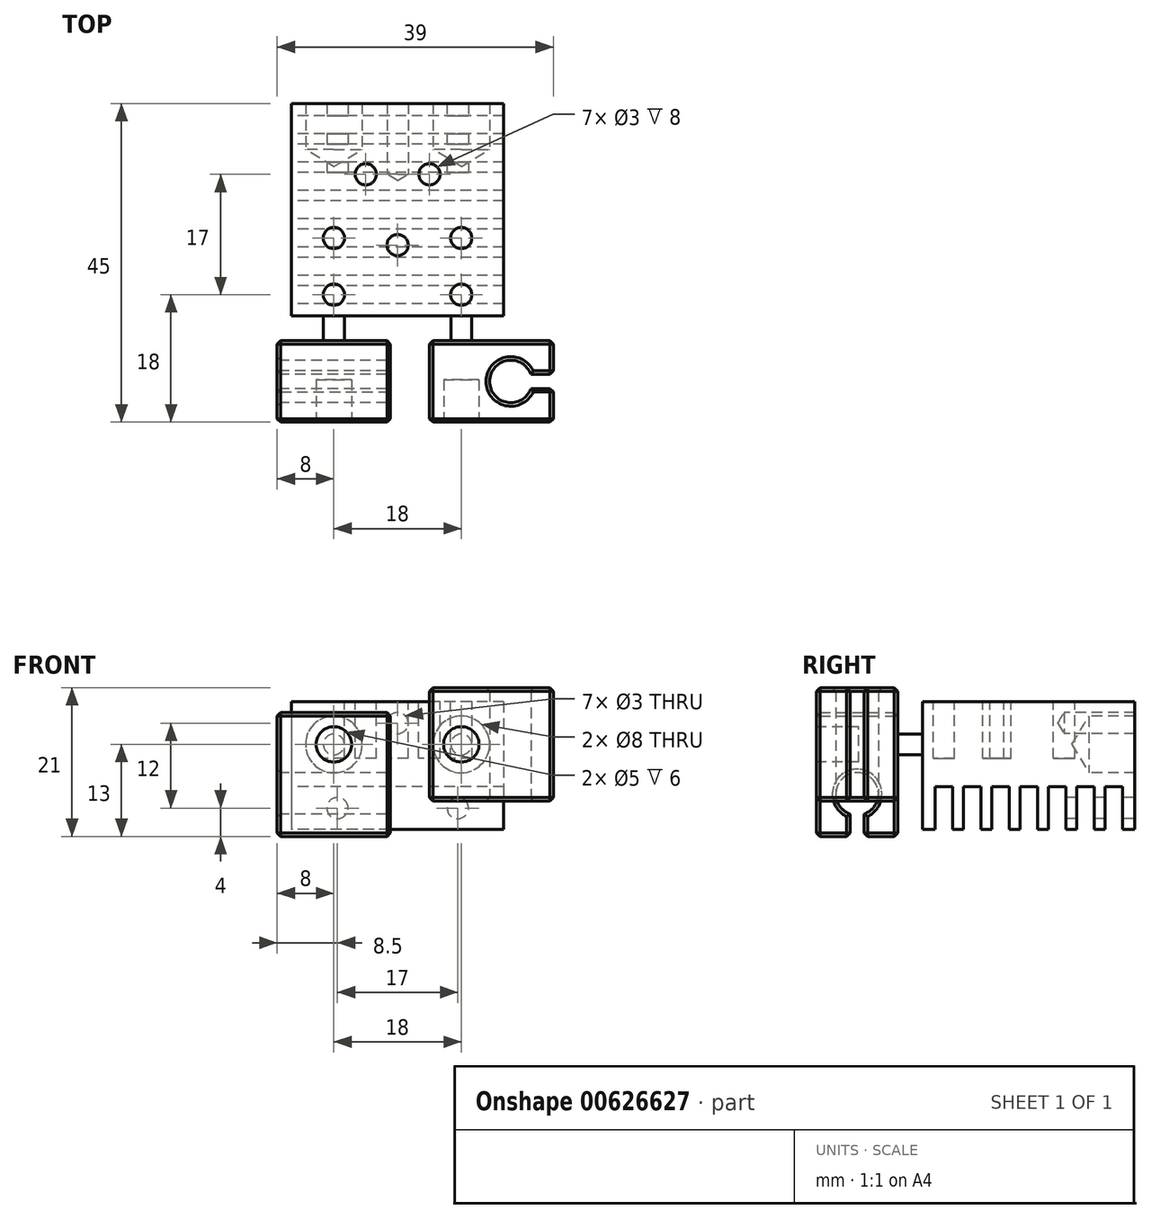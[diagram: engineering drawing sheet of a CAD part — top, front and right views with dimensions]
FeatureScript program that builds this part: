
annotation { "Feature Type Name" : "Feature", "Feature Type Description" : "" }
export const myFeature = defineFeature(function(context is Context, id is Id, definition is map)
    precondition{}
    {
        {
            var Q0;
            Q0=qCreatedBy(makeId("Top.planeOp"),FACE);
            var sketch = newSketch(context, id + "F0", { "sketchPlane" : qUnion([Q0])});
            skLineSegment(sketch, "E0.bottom", {"start": v(15, -15) * mm, "end": v(-15, -15) * mm});
            skLineSegment(sketch, "E0.top", {"start": v(15, 15) * mm, "end": v(-15, 15) * mm});
            skLineSegment(sketch, "E0.left", {"start": v(15, -15) * mm, "end": v(15, 15) * mm});
            skLineSegment(sketch, "E0.right", {"start": v(-15, -15) * mm, "end": v(-15, 15) * mm});
            skPoint(sketch, "E0.middle", {"position": v(0, 0) * mm});
            skSolve(sketch);
        }
        {
            var Q0;
            Q0=makeQuery(id+"F0.imprint","IMPRINT",FACE,{"disambiguationData":[TD([[makeQuery(id+"F0.imprint","IMPRINT",EDGE,{"derivedFrom":sQuery(id+"F0.wireOp",EDGE,"E0.bottom")}),-1.0]])]});
            extrude(context, id + "F11", {"entities" : qUnion([Q0]), "depth" : 18 * mm});
        }
        {
            var Q0;
            Q0=makeQuery(id+"F11.opExtrude","SWEPT_FACE",FACE,{"disambiguationData":[OSD([sQuery(id+"F0.wireOp",EDGE,"E0.top")])]});
            var sketch = newSketch(context, id + "F12", { "sketchPlane" : qUnion([Q0])});
            skPoint(sketch, "E1", {"position": v(-8.5, 3) * mm});
            skPoint(sketch, "E2", {"position": v(8.5, 3) * mm});
            skPoint(sketch, "E3", {"position": v(-9, 12) * mm});
            skPoint(sketch, "E4", {"position": v(9, 12) * mm});
            skPoint(sketch, "E5", {"position": v(0, 15) * mm});
            skSolve(sketch);
        }
        {
            var Q0;
            Q0=sQuery(id+"F12.wireOp",VERTEX,"E3");
            var Q1;
            Q1=sQuery(id+"F12.wireOp",VERTEX,"E4");
            var Q2;
            Q2=makeQuery(id+"F11.opExtrude","SWEPT_BODY",BODY,{"disambiguationData":[OSD([sQuery(id+"F0.wireOp",EDGE,"E0.bottom"),sQuery(id+"F0.wireOp",EDGE,"E0.top"),sQuery(id+"F0.wireOp",EDGE,"E0.left"),sQuery(id+"F0.wireOp",EDGE,"E0.right")])]});
            hole(context, id + "F1", {"style" : HoleStyle.SIMPLE, "endStyle" : HoleEndStyle.BLIND, "holeDiameter" : 8 * mm, "holeDepth" : 6.5 * mm, "locations" : qUnion([Q0, Q1]), "scope" : qUnion([Q2]), "tappedDepth" : 12 * mm, "tapClearance" : 3});
        }
        {
            var Q0;
            Q0=makeQuery(id+"F11.opExtrude","CAP_FACE",FACE,{"disambiguationData":[OSD([sQuery(id+"F0.wireOp",EDGE,"E0.bottom"),sQuery(id+"F0.wireOp",EDGE,"E0.top"),sQuery(id+"F0.wireOp",EDGE,"E0.left"),sQuery(id+"F0.wireOp",EDGE,"E0.right")])],"isStart":true});
            var sketch = newSketch(context, id + "F13", { "sketchPlane" : qUnion([Q0])});
            skLineSegment(sketch, "E6.bottom", {"start": v(15, -13.25) * mm, "end": v(-15.01, -13.25) * mm});
            skLineSegment(sketch, "E6.top", {"start": v(15, -10.75) * mm, "end": v(-15.01, -10.75) * mm});
            skLineSegment(sketch, "E6.left", {"start": v(15, -13.25) * mm, "end": v(15, -10.75) * mm});
            skLineSegment(sketch, "E6.right", {"start": v(-15.01, -13.25) * mm, "end": v(-15.01, -10.75) * mm});
            skLineSegment(sketch, "E7.0.1.0", {"start": v(15, -9.25) * mm, "end": v(15, -6.75) * mm});
            skLineSegment(sketch, "E7.0.1.1", {"start": v(-15.01, -9.25) * mm, "end": v(-15.01, -6.75) * mm});
            skLineSegment(sketch, "E7.0.1.2", {"start": v(15, -9.25) * mm, "end": v(-15.01, -9.25) * mm});
            skLineSegment(sketch, "E7.0.1.3", {"start": v(15, -6.75) * mm, "end": v(-15.01, -6.75) * mm});
            skLineSegment(sketch, "E7.0.2.0", {"start": v(15, -5.25) * mm, "end": v(15, -2.75) * mm});
            skLineSegment(sketch, "E7.0.2.1", {"start": v(-15.01, -5.25) * mm, "end": v(-15.01, -2.75) * mm});
            skLineSegment(sketch, "E7.0.2.2", {"start": v(15, -5.25) * mm, "end": v(-15.01, -5.25) * mm});
            skLineSegment(sketch, "E7.0.2.3", {"start": v(15, -2.75) * mm, "end": v(-15.01, -2.75) * mm});
            skLineSegment(sketch, "E7.0.3.0", {"start": v(15, -1.25) * mm, "end": v(15, 1.25) * mm});
            skLineSegment(sketch, "E7.0.3.1", {"start": v(-15.01, -1.25) * mm, "end": v(-15.01, 1.25) * mm});
            skLineSegment(sketch, "E7.0.3.2", {"start": v(15, -1.25) * mm, "end": v(-15.01, -1.25) * mm});
            skLineSegment(sketch, "E7.0.3.3", {"start": v(15, 1.25) * mm, "end": v(-15.01, 1.25) * mm});
            skLineSegment(sketch, "E7.0.4.0", {"start": v(15, 2.75) * mm, "end": v(15, 5.25) * mm});
            skLineSegment(sketch, "E7.0.4.1", {"start": v(-15.01, 2.75) * mm, "end": v(-15.01, 5.25) * mm});
            skLineSegment(sketch, "E7.0.4.2", {"start": v(15, 2.75) * mm, "end": v(-15.01, 2.75) * mm});
            skLineSegment(sketch, "E7.0.4.3", {"start": v(15, 5.25) * mm, "end": v(-15.01, 5.25) * mm});
            skLineSegment(sketch, "E7.0.5.0", {"start": v(15, 6.75) * mm, "end": v(15, 9.25) * mm});
            skLineSegment(sketch, "E7.0.5.1", {"start": v(-15.01, 6.75) * mm, "end": v(-15.01, 9.25) * mm});
            skLineSegment(sketch, "E7.0.5.2", {"start": v(15, 6.75) * mm, "end": v(-15.01, 6.75) * mm});
            skLineSegment(sketch, "E7.0.5.3", {"start": v(15, 9.25) * mm, "end": v(-15.01, 9.25) * mm});
            skLineSegment(sketch, "E7.0.6.0", {"start": v(15, 10.75) * mm, "end": v(15, 13.25) * mm});
            skLineSegment(sketch, "E7.0.6.1", {"start": v(-15.01, 10.75) * mm, "end": v(-15.01, 13.25) * mm});
            skLineSegment(sketch, "E7.0.6.2", {"start": v(15, 10.75) * mm, "end": v(-15.01, 10.75) * mm});
            skLineSegment(sketch, "E7.0.6.3", {"start": v(15, 13.25) * mm, "end": v(-15.01, 13.25) * mm});
            skLineSegment(sketch, "E7.direction1", {"start": v(-15.01, -13.25) * mm, "end": v(9.99, -13.25) * mm, "construction": true});
            skLineSegment(sketch, "E7.direction2", {"start": v(-15.01, -13.25) * mm, "end": v(-15.01, -9.25) * mm, "construction": true});
            skSolve(sketch);
        }
        {
            var Q0;
            {var subQ0=sQuery(id+"F13.wireOp",EDGE,"E7.0.6.0");Q0=makeQuery(id+"F13.imprint","IMPRINT",FACE,{"disambiguationData":[TD([[makeQuery(id+"F13.imprint","IMPRINT",EDGE,{"derivedFrom":subQ0}),-1.0]])]});}
            var Q1;
            {var subQ0=sQuery(id+"F13.wireOp",EDGE,"E7.0.5.0");Q1=makeQuery(id+"F13.imprint","IMPRINT",FACE,{"disambiguationData":[TD([[makeQuery(id+"F13.imprint","IMPRINT",EDGE,{"derivedFrom":subQ0}),-1.0]])]});}
            var Q2;
            {var subQ0=sQuery(id+"F13.wireOp",EDGE,"E7.0.4.0");Q2=makeQuery(id+"F13.imprint","IMPRINT",FACE,{"disambiguationData":[TD([[makeQuery(id+"F13.imprint","IMPRINT",EDGE,{"derivedFrom":subQ0}),-1.0]])]});}
            var Q3;
            {var subQ0=sQuery(id+"F13.wireOp",EDGE,"E7.0.3.0");Q3=makeQuery(id+"F13.imprint","IMPRINT",FACE,{"disambiguationData":[TD([[makeQuery(id+"F13.imprint","IMPRINT",EDGE,{"derivedFrom":subQ0}),-1.0]])]});}
            var Q4;
            {var subQ0=sQuery(id+"F13.wireOp",EDGE,"E7.0.2.0");Q4=makeQuery(id+"F13.imprint","IMPRINT",FACE,{"disambiguationData":[TD([[makeQuery(id+"F13.imprint","IMPRINT",EDGE,{"derivedFrom":subQ0}),-1.0]])]});}
            var Q5;
            {var subQ0=sQuery(id+"F13.wireOp",EDGE,"E7.0.1.0");Q5=makeQuery(id+"F13.imprint","IMPRINT",FACE,{"disambiguationData":[TD([[makeQuery(id+"F13.imprint","IMPRINT",EDGE,{"derivedFrom":subQ0}),-1.0]])]});}
            var Q6;
            {var subQ0=sQuery(id+"F13.wireOp",EDGE,"E6.left");Q6=makeQuery(id+"F13.imprint","IMPRINT",FACE,{"disambiguationData":[TD([[makeQuery(id+"F13.imprint","IMPRINT",EDGE,{"derivedFrom":subQ0}),-1.0]])]});}
            extrude(context, id + "F14", {"entities" : qUnion([Q0, Q1, Q2, Q3, Q4, Q5, Q6]), "operationType" : NewBodyOperationType.REMOVE, "oppositeDirection" : true, "depth" : 6 * mm});
        }
        {
            var Q0;
            Q0=sQuery(id+"F12.wireOp",VERTEX,"E2");
            var Q1;
            Q1=sQuery(id+"F12.wireOp",VERTEX,"E1");
            var Q2;
            Q2=sQuery(id+"F12.wireOp",VERTEX,"E5");
            var Q3;
            Q3=makeQuery(id+"F11.opExtrude","SWEPT_BODY",BODY,{"disambiguationData":[OSD([sQuery(id+"F0.wireOp",EDGE,"E0.bottom"),sQuery(id+"F0.wireOp",EDGE,"E0.top"),sQuery(id+"F0.wireOp",EDGE,"E0.left"),sQuery(id+"F0.wireOp",EDGE,"E0.right")])]});
            hole(context, id + "F15", {"style" : HoleStyle.SIMPLE, "endStyle" : HoleEndStyle.BLIND, "holeDiameter" : 3 * mm, "holeDepth" : 10 * mm, "locations" : qUnion([Q0, Q1, Q2]), "scope" : qUnion([Q3])});
        }
        {
            var Q0;
            Q0=makeQuery(id+"F11.opExtrude","SWEPT_FACE",FACE,{"disambiguationData":[OSD([sQuery(id+"F0.wireOp",EDGE,"E0.bottom")])]});
            var sketch = newSketch(context, id + "F2", { "sketchPlane" : qUnion([Q0])});
            skCircle(sketch, "E8", {"center": v(9, 12) * mm, "radius": 1.48 * mm});
            skCircle(sketch, "E9", {"center": v(-9, 12) * mm, "radius": 1.48 * mm});
            skLineSegment(sketch, "E10", {"start": v(-15, 12) * mm, "end": v(15, 12) * mm, "construction": true});
            skSolve(sketch);
        }
        {
            var Q0;
            Q0=makeQuery(id+"F2.imprint","IMPRINT",FACE,{"disambiguationData":[TD([[makeQuery(id+"F2.imprint","IMPRINT",EDGE,{"derivedFrom":sQuery(id+"F2.wireOp",EDGE,"E9")}),1.0]])]});
            var Q1;
            Q1=makeQuery(id+"F2.imprint","IMPRINT",FACE,{"disambiguationData":[TD([[makeQuery(id+"F2.imprint","IMPRINT",EDGE,{"derivedFrom":sQuery(id+"F2.wireOp",EDGE,"E8")}),1.0]])]});
            extrude(context, id + "F3", {"entities" : qUnion([Q0, Q1]), "operationType" : NewBodyOperationType.ADD, "depth" : 3.5 * mm});
        }
        {
            var Q0;
            Q0=makeQuery(id+"F3.opExtrude","CAP_FACE",FACE,{"disambiguationData":[OSD([sQuery(id+"F2.wireOp",EDGE,"E8")])],"isStart":false});
            var sketch = newSketch(context, id + "F16", { "sketchPlane" : qUnion([Q0])});
            skLineSegment(sketch, "E11.bottom", {"start": v(22, 20) * mm, "end": v(22, 4) * mm});
            skLineSegment(sketch, "E11.top", {"start": v(4.5, 20) * mm, "end": v(4.5, 4) * mm});
            skLineSegment(sketch, "E11.left", {"start": v(22, 20) * mm, "end": v(4.5, 20) * mm});
            skLineSegment(sketch, "E11.right", {"start": v(22, 4) * mm, "end": v(4.5, 4) * mm});
            skPoint(sketch, "E12", {"position": v(9, 12) * mm});
            skLineSegment(sketch, "E13", {"start": v(4.5, 12) * mm, "end": v(22, 12) * mm, "construction": true});
            skSolve(sketch);
        }
        {
            var Q0;
            Q0=makeQuery(id+"F3.opExtrude","CAP_FACE",FACE,{"disambiguationData":[OSD([sQuery(id+"F2.wireOp",EDGE,"E9")])],"isStart":false});
            var sketch = newSketch(context, id + "F17", { "sketchPlane" : qUnion([Q0])});
            skPoint(sketch, "E14", {"position": v(-9, 12) * mm});
            skLineSegment(sketch, "E15.bottom", {"start": v(-17, 16.5) * mm, "end": v(-1, 16.5) * mm});
            skLineSegment(sketch, "E15.top", {"start": v(-17, -1) * mm, "end": v(-1, -1) * mm});
            skLineSegment(sketch, "E15.left", {"start": v(-17, 16.5) * mm, "end": v(-17, -1) * mm});
            skLineSegment(sketch, "E15.right", {"start": v(-1, 16.5) * mm, "end": v(-1, -1) * mm});
            skLineSegment(sketch, "E16", {"start": v(-9, 16.5) * mm, "end": v(-9, -1) * mm, "construction": true});
            skSolve(sketch);
        }
        {
            var Q0;
            Q0=qSketchRegion(id+"F17",true);
            var Q1;
            Q1=qSketchRegion(id+"F16",true);
            extrude(context, id + "F18", {"entities" : qUnion([Q0, Q1]), "operationType" : NewBodyOperationType.ADD, "depth" : 11.5 * mm});
        }
        {
            var Q0;
            Q0=makeQuery(id+"F18.opExtrude","CAP_FACE",FACE,{"disambiguationData":[OSD([sQuery(id+"F16.wireOp",EDGE,"E11.bottom"),sQuery(id+"F16.wireOp",EDGE,"E11.top"),sQuery(id+"F16.wireOp",EDGE,"E11.left"),sQuery(id+"F16.wireOp",EDGE,"E11.right")])],"isStart":false});
            var sketch = newSketch(context, id + "F19", { "sketchPlane" : qUnion([Q0])});
            skCircle(sketch, "E17", {"center": v(9, 12) * mm, "radius": 2.5 * mm});
            skSolve(sketch);
        }
        {
            var Q0;
            Q0=makeQuery(id+"F18.opExtrude","CAP_FACE",FACE,{"disambiguationData":[OSD([sQuery(id+"F17.wireOp",EDGE,"E15.bottom"),sQuery(id+"F17.wireOp",EDGE,"E15.top"),sQuery(id+"F17.wireOp",EDGE,"E15.left"),sQuery(id+"F17.wireOp",EDGE,"E15.right")])],"isStart":false});
            var sketch = newSketch(context, id + "F20", { "sketchPlane" : qUnion([Q0])});
            skCircle(sketch, "E18", {"center": v(-9, 12) * mm, "radius": 2.5 * mm});
            skSolve(sketch);
        }
        {
            var Q0;
            Q0=makeQuery(id+"F18.opExtrude","SWEPT_FACE",FACE,{"disambiguationData":[OSD([sQuery(id+"F16.wireOp",EDGE,"E11.right")])]});
            var sketch = newSketch(context, id + "F4", { "sketchPlane" : qUnion([Q0])});
            skArc(sketch, "E19", {"start": v(18.83, 25.25) * mm, "mid": v(13, 24.25) * mm, "end": v(18.83, 23.25) * mm});
            skLineSegment(sketch, "E20.bottom", {"start": v(22, 25.25) * mm, "end": v(22, 23.25) * mm});
            skLineSegment(sketch, "E20.left", {"start": v(22, 25.25) * mm, "end": v(18.83, 25.25) * mm});
            skLineSegment(sketch, "E20.right", {"start": v(22, 23.25) * mm, "end": v(18.83, 23.25) * mm});
            skLineSegment(sketch, "E21", {"start": v(16, 24.25) * mm, "end": v(22, 24.25) * mm, "construction": true});
            skSolve(sketch);
        }
        {
            var Q0;
            {var subQ0=sQuery(id+"F4.wireOp",EDGE,"E19");Q0=makeQuery(id+"F4.imprint","IMPRINT",FACE,{"disambiguationData":[TD([[makeQuery(id+"F4.imprint","IMPRINT",EDGE,{"derivedFrom":subQ0}),1.0]])]});}
            extrude(context, id + "F5", {"entities" : qUnion([Q0]), "operationType" : NewBodyOperationType.REMOVE, "endBound" : BoundingType.UP_TO_NEXT, "oppositeDirection" : true, "depth" : 25 * mm});
        }
        {
            var Q0;
            Q0=makeQuery(id+"F18.opExtrude","SWEPT_FACE",FACE,{"disambiguationData":[OSD([sQuery(id+"F17.wireOp",EDGE,"E15.left")])]});
            var sketch = newSketch(context, id + "F6", { "sketchPlane" : qUnion([Q0])});
            skArc(sketch, "E22", {"start": v(25.25, 2.17) * mm, "mid": v(24.25, 8) * mm, "end": v(23.25, 2.17) * mm});
            skLineSegment(sketch, "E23.bottom", {"start": v(25.25, -1) * mm, "end": v(23.25, -1) * mm});
            skLineSegment(sketch, "E23.left", {"start": v(25.25, -1) * mm, "end": v(25.25, 2.17) * mm});
            skLineSegment(sketch, "E23.right", {"start": v(23.25, -1) * mm, "end": v(23.25, 2.17) * mm});
            skLineSegment(sketch, "E24", {"start": v(24.25, 5) * mm, "end": v(24.25, -1) * mm, "construction": true});
            skSolve(sketch);
        }
        {
            var Q0;
            {var subQ1=sQuery(id+"F6.wireOp",EDGE,"a5043bc3-80df-4e10-9600-923cc40a1bd6");var subQ9=makeQuery(id+"F6.imprint","IMPRINT",VERTEX,{"derivedFrom":subQ1});Q0=makeQuery(id+"F6.imprint","IMPRINT",FACE,{"disambiguationData":[TD([[makeQuery(id+"F6.imprint","IMPRINT",EDGE,{"disambiguationData":[TD([[subQ9,1.0]])],"derivedFrom":subQ1}),1.0]])]});}
            var Q1;
            {var subQ0=sQuery(id+"F6.wireOp",EDGE,"8e0e61a6-ac7d-4fc6-8048-e39d4b8b92de.top");Q1=makeQuery(id+"F6.imprint","IMPRINT",FACE,{"disambiguationData":[TD([[makeQuery(id+"F6.imprint","IMPRINT",EDGE,{"derivedFrom":subQ0}),-1.0]])]});}
            var Q2;
            Q2=makeQuery(id+"F6.imprint","IMPRINT",FACE,{"disambiguationData":[TD([[makeQuery(id+"F6.imprint","IMPRINT",EDGE,{"derivedFrom":sQuery(id+"F6.wireOp",EDGE,"E22")}),1.0]])]});
            extrude(context, id + "F21", {"entities" : qUnion([Q0, Q1, Q2]), "operationType" : NewBodyOperationType.REMOVE, "endBound" : BoundingType.UP_TO_NEXT, "oppositeDirection" : true, "depth" : 25 * mm});
        }
        {
            var Q0;
            Q0=makeQuery(id+"F11.opExtrude","CAP_FACE",FACE,{"disambiguationData":[OSD([sQuery(id+"F0.wireOp",EDGE,"E0.bottom"),sQuery(id+"F0.wireOp",EDGE,"E0.top"),sQuery(id+"F0.wireOp",EDGE,"E0.left"),sQuery(id+"F0.wireOp",EDGE,"E0.right")])],"isStart":false});
            var sketch = newSketch(context, id + "F7", { "sketchPlane" : qUnion([Q0])});
            skLineSegment(sketch, "E25", {"start": v(-15, -12) * mm, "end": v(15, -12) * mm, "construction": true});
            skLineSegment(sketch, "E26", {"start": v(-15, -4) * mm, "end": v(15, -4) * mm, "construction": true});
            skLineSegment(sketch, "E27", {"start": v(-15, 5) * mm, "end": v(15, 5) * mm, "construction": true});
            skLineSegment(sketch, "E28", {"start": v(-15, -5) * mm, "end": v(15, -5) * mm, "construction": true});
            skLineSegment(sketch, "E29", {"start": v(0, -15) * mm, "end": v(0, 15) * mm, "construction": true});
            skCircle(sketch, "E30", {"center": v(0, -5) * mm, "radius": 1.5 * mm});
            skCircle(sketch, "E31", {"center": v(-4.5, 5) * mm, "radius": 1.5 * mm});
            skCircle(sketch, "E32", {"center": v(4.5, 5) * mm, "radius": 1.5 * mm});
            skCircle(sketch, "E33", {"center": v(-9, -12) * mm, "radius": 1.5 * mm});
            skCircle(sketch, "E34", {"center": v(-9, -4) * mm, "radius": 1.5 * mm});
            skCircle(sketch, "E35", {"center": v(9, -12) * mm, "radius": 1.5 * mm});
            skCircle(sketch, "E36", {"center": v(9, -4) * mm, "radius": 1.5 * mm});
            skSolve(sketch);
        }
        {
            var Q0;
            Q0=makeQuery(id+"F18.opExtrude","SWEPT_FACE",FACE,{"disambiguationData":[OSD([sQuery(id+"F16.wireOp",EDGE,"E11.right")])]});
            var Q1;
            Q1=makeQuery(id+"F18.opExtrude","SWEPT_FACE",FACE,{"disambiguationData":[OSD([sQuery(id+"F16.wireOp",EDGE,"E11.top")])]});
            var Q2;
            Q2=makeQuery(id+"F18.opExtrude","SWEPT_FACE",FACE,{"disambiguationData":[OSD([sQuery(id+"F17.wireOp",EDGE,"E15.top")])]});
            var Q3;
            Q3=makeQuery(id+"F18.opExtrude","SWEPT_FACE",FACE,{"disambiguationData":[OSD([sQuery(id+"F17.wireOp",EDGE,"E15.right")])]});
            var Q4;
            {var subQ2=sQuery(id+"F16.wireOp",EDGE,"E11.bottom");Q4=makeQuery(id+"F5.boolean.opBoolean","SPLIT",FACE,{"disambiguationData":[TD([makeQuery(id+"F5.opExtrude","SWEPT_FACE",FACE,{"disambiguationData":[OSD([sQuery(id+"F4.wireOp",EDGE,"E20.right")])]})])],"derivedFrom":makeQuery(id+"F18.opExtrude","SWEPT_FACE",FACE,{"disambiguationData":[OSD([subQ2])]})});}
            var Q5;
            {var subQ2=sQuery(id+"F16.wireOp",EDGE,"E11.bottom");Q5=makeQuery(id+"F5.boolean.opBoolean","SPLIT",FACE,{"disambiguationData":[TD([makeQuery(id+"F5.opExtrude","SWEPT_FACE",FACE,{"disambiguationData":[OSD([sQuery(id+"F4.wireOp",EDGE,"E20.left")])]})])],"derivedFrom":makeQuery(id+"F18.opExtrude","SWEPT_FACE",FACE,{"disambiguationData":[OSD([subQ2])]})});}
            var Q6;
            Q6=makeQuery(id+"F18.opExtrude","SWEPT_FACE",FACE,{"disambiguationData":[OSD([sQuery(id+"F17.wireOp",EDGE,"E15.bottom")])]});
            var Q7;
            Q7=makeQuery(id+"F18.opExtrude","SWEPT_FACE",FACE,{"disambiguationData":[OSD([sQuery(id+"F17.wireOp",EDGE,"E15.left")])]});
            var Q8;
            Q8=makeQuery(id+"F18.opExtrude","SWEPT_FACE",FACE,{"disambiguationData":[OSD([sQuery(id+"F16.wireOp",EDGE,"E11.left")])]});
            chamfer(context, id + "F8", {"entities" : qUnion([Q0, Q1, Q2, Q3, Q4, Q5, Q6, Q7, Q8]), "width" : 0.5 * mm, "tangentPropagation" : true});
        }
        {
            var Q0;
            Q0=makeQuery(id+"F7.imprint","IMPRINT",FACE,{"disambiguationData":[TD([[makeQuery(id+"F7.imprint","IMPRINT",EDGE,{"derivedFrom":sQuery(id+"F7.wireOp",EDGE,"E33")}),1.0]])]});
            var Q1;
            Q1=makeQuery(id+"F7.imprint","IMPRINT",FACE,{"disambiguationData":[TD([[makeQuery(id+"F7.imprint","IMPRINT",EDGE,{"derivedFrom":sQuery(id+"F7.wireOp",EDGE,"E34")}),1.0]])]});
            var Q2;
            Q2=makeQuery(id+"F7.imprint","IMPRINT",FACE,{"disambiguationData":[TD([[makeQuery(id+"F7.imprint","IMPRINT",EDGE,{"derivedFrom":sQuery(id+"F7.wireOp",EDGE,"E30")}),1.0]])]});
            var Q3;
            Q3=makeQuery(id+"F7.imprint","IMPRINT",FACE,{"disambiguationData":[TD([[makeQuery(id+"F7.imprint","IMPRINT",EDGE,{"derivedFrom":sQuery(id+"F7.wireOp",EDGE,"E32")}),1.0]])]});
            var Q4;
            Q4=makeQuery(id+"F7.imprint","IMPRINT",FACE,{"disambiguationData":[TD([[makeQuery(id+"F7.imprint","IMPRINT",EDGE,{"derivedFrom":sQuery(id+"F7.wireOp",EDGE,"E36")}),1.0]])]});
            var Q5;
            Q5=makeQuery(id+"F7.imprint","IMPRINT",FACE,{"disambiguationData":[TD([[makeQuery(id+"F7.imprint","IMPRINT",EDGE,{"derivedFrom":sQuery(id+"F7.wireOp",EDGE,"E35")}),1.0]])]});
            var Q6;
            Q6=makeQuery(id+"F7.imprint","IMPRINT",FACE,{"disambiguationData":[TD([[makeQuery(id+"F7.imprint","IMPRINT",EDGE,{"derivedFrom":sQuery(id+"F7.wireOp",EDGE,"E31")}),1.0]])]});
            extrude(context, id + "F9", {"entities" : qUnion([Q0, Q1, Q2, Q3, Q4, Q5, Q6]), "operationType" : NewBodyOperationType.REMOVE, "oppositeDirection" : true, "depth" : 8 * mm});
        }
        {
            var Q0;
            Q0=makeQuery(id+"F20.imprint","IMPRINT",FACE,{"disambiguationData":[TD([[makeQuery(id+"F20.imprint","IMPRINT",EDGE,{"derivedFrom":sQuery(id+"F20.wireOp",EDGE,"E18")}),1.0]])]});
            var Q1;
            Q1=makeQuery(id+"F19.imprint","IMPRINT",FACE,{"disambiguationData":[TD([[makeQuery(id+"F19.imprint","IMPRINT",EDGE,{"derivedFrom":sQuery(id+"F19.wireOp",EDGE,"E17")}),1.0]])]});
            extrude(context, id + "F10", {"entities" : qUnion([Q0, Q1]), "operationType" : NewBodyOperationType.REMOVE, "oppositeDirection" : true, "depth" : 6 * mm});
        }
    });
